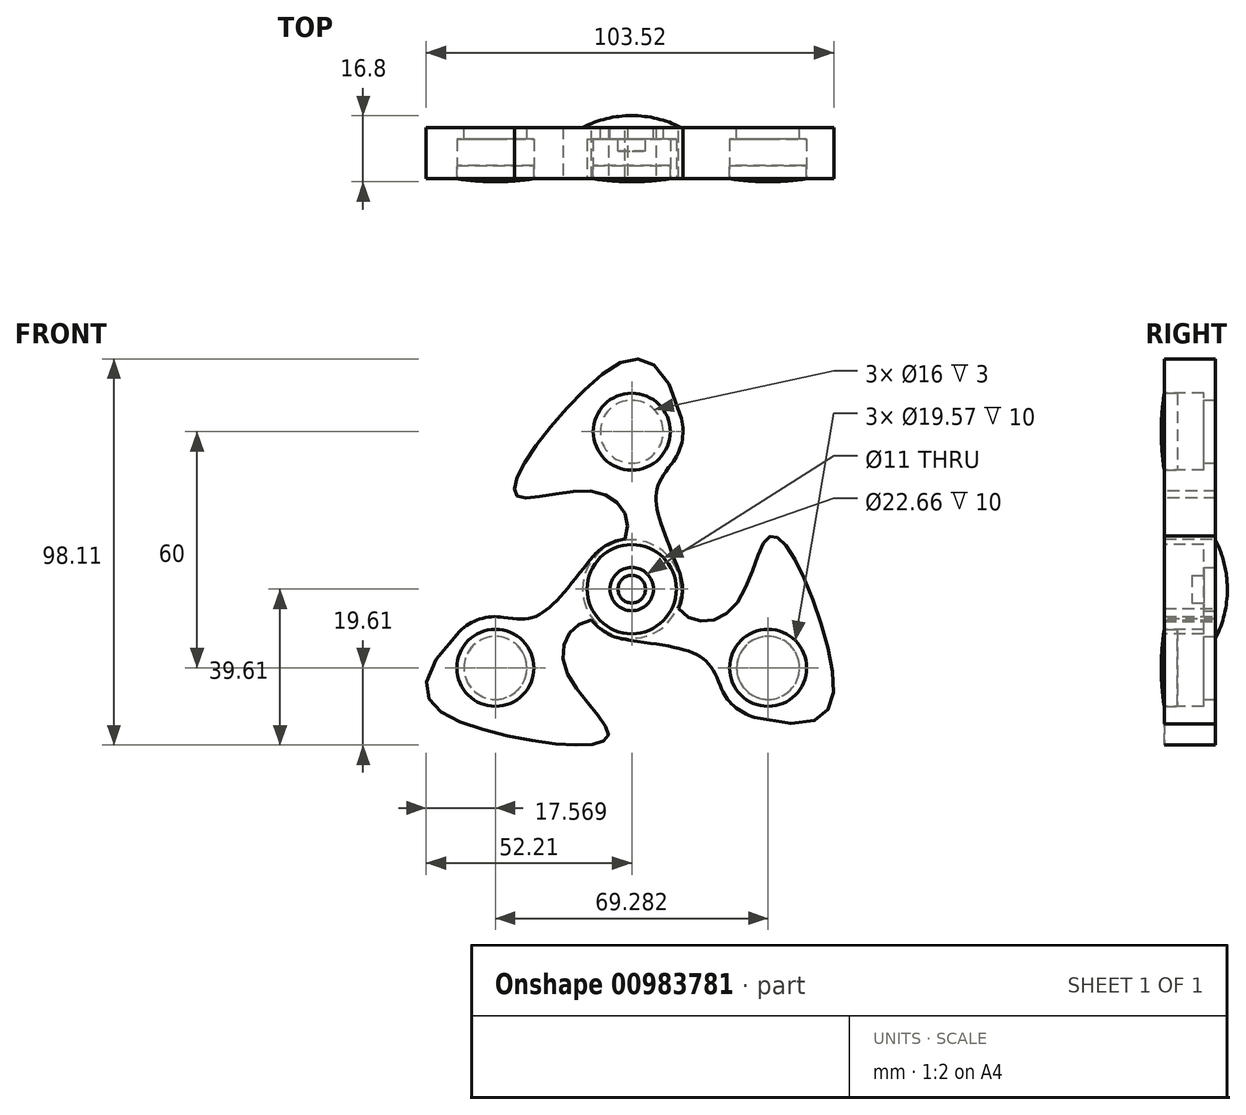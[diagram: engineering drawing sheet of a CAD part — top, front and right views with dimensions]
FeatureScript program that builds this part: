
annotation { "Feature Type Name" : "Feature", "Feature Type Description" : "" }
export const myFeature = defineFeature(function(context is Context, id is Id, definition is map)
    precondition{}
    {
        {
            var Q0;
            Q0=qCreatedBy(makeId("Right.planeOp"),FACE);
            var sketch = newSketch(context, id + "F0", { "sketchPlane" : qUnion([Q0])});
            skLineSegment(sketch, "E0", {"start": v(55.37, 0) * mm, "end": v(-57.34, 0) * mm, "construction": true});
            skSolve(sketch);
        }
        {
            var Q0;
            Q0=qCreatedBy(makeId("Front.planeOp"),FACE);
            var sketch = newSketch(context, id + "F1", { "sketchPlane" : qUnion([Q0])});
            skArc(sketch, "E1", {"start": v(10.1, 31.81) * mm, "mid": v(12.7, 37.26) * mm, "end": v(12.57, 43.3) * mm});
            skArc(sketch, "E2", {"start": v(-12.75, -1.81) * mm, "mid": v(3.2, -12.47) * mm, "end": v(12.04, 4.56) * mm});
            skFitSpline(sketch, "E3", {"points": [v(12.57, 43.3) * mm, v(-13, 49.56) * mm, v(-29.24, 23.79) * mm, v(-8.86, 24.65) * mm, v(-1.57, 13.14) * mm, v(-12.75, -1.81) * mm], "startDerivative": vector(-80.86, 308.24) * mm, "endDerivative": vector(8.65, -60.88) * mm});
            skFitSpline(sketch, "E4", {"points": [v(10.1, 31.81) * mm, v(6.13, 23.11) * mm, v(12.04, 4.56) * mm], "startDerivative": vector(-18.49, -22.8) * mm, "endDerivative": vector(14.68, -38.75) * mm});
            skCircle(sketch, "E5", {"center": v(0, 0) * mm, "radius": 5.5 * mm});
            skCircle(sketch, "E6", {"center": v(0, 40) * mm, "radius": 8 * mm});
            skSolve(sketch);
        }
        {
            var Q0;
            Q0 = qSketchRegion(id + "F1", true);
            extrude(context, id + "F2", {"entities" : qUnion([Q0]), "depth" : 13 * mm, "offsetDistance" : 25 * mm});
        }
        {
            var Q0;
            Q0=makeQuery(id+"F2.opExtrude","SWEPT_BODY",BODY,{"disambiguationData":[OSD([sQuery(id+"F1.wireOp",EDGE,"E1"),sQuery(id+"F1.wireOp",EDGE,"E2"),sQuery(id+"F1.wireOp",EDGE,"E3"),sQuery(id+"F1.wireOp",EDGE,"E4"),sQuery(id+"F1.wireOp",EDGE,"E5"),sQuery(id+"F1.wireOp",EDGE,"E6")])]});
            var Q1;
            Q1=sQuery(id+"F0.wireOp",EDGE,"E0");
            circularPattern(context, id + "F3", {"operationType" : NewBodyOperationType.ADD, "entities" : qUnion([Q0]), "axis" : qUnion([Q1]), "angle" : 360 * degree, "instanceCount" : 3, "equalSpace" : true});
        }
        {
            var Q0;
            {var subQ0=makeQuery(id+"F2.opExtrude","CAP_FACE",FACE,{"disambiguationData":[OSD([sQuery(id+"F1.wireOp",EDGE,"E1"),sQuery(id+"F1.wireOp",EDGE,"E2"),sQuery(id+"F1.wireOp",EDGE,"E3"),sQuery(id+"F1.wireOp",EDGE,"E4"),sQuery(id+"F1.wireOp",EDGE,"E5"),sQuery(id+"F1.wireOp",EDGE,"E6")])],"isStart":false});Q0=makeQuery(id+"F3.boolean.opBoolean","MERGE",FACE,{"derivedFrom":[subQ0,makeQuery(id+"F3.opPattern","COPY",FACE,{"derivedFrom":subQ0,"instanceName":"1"}),makeQuery(id+"F3.opPattern","COPY",FACE,{"derivedFrom":subQ0,"instanceName":"2"})]});}
            var sketch = newSketch(context, id + "F4", { "sketchPlane" : qUnion([Q0])});
            skCircle(sketch, "E7", {"center": v(0, 0) * mm, "radius": 11.33 * mm});
            skCircle(sketch, "E8.0", {"center": v(0, 40) * mm, "radius": 8 * mm, "construction": true});
            skCircle(sketch, "E9", {"center": v(0, 40) * mm, "radius": 9.79 * mm});
            skCircle(sketch, "E10", {"center": v(-34.64, -20) * mm, "radius": 9.79 * mm});
            skCircle(sketch, "E11", {"center": v(34.64, -20) * mm, "radius": 9.79 * mm});
            skCircle(sketch, "E12.0", {"center": v(-34.64, -20) * mm, "radius": 8 * mm, "construction": true});
            skCircle(sketch, "E13.0", {"center": v(34.64, -20) * mm, "radius": 8 * mm, "construction": true});
            skSolve(sketch);
        }
        {
            var Q0;
            Q0 = qSketchRegion(id + "F4", true);
            extrude(context, id + "F5", {"entities" : qUnion([Q0]), "operationType" : NewBodyOperationType.REMOVE, "oppositeDirection" : true, "depth" : 10 * mm, "offsetDistance" : 25 * mm});
        }
        {
            var Q0;
            Q0=qCreatedBy(makeId("Right.planeOp"),FACE);
            var sketch = newSketch(context, id + "F6", { "sketchPlane" : qUnion([Q0])});
            skPoint(sketch, "E14.0", {"position": v(0, 40) * mm});
            skLineSegment(sketch, "E15.0.0", {"start": v(-13, 11.33) * mm, "end": v(-13, -11.33) * mm, "construction": true});
            skFitSpline(sketch, "E15.0.1", {"points": [v(-13, 1.74) * mm, v(-13, 0.56) * mm, v(-13, -0.63) * mm, v(-13, -1.81) * mm], "construction": true});
            skLineSegment(sketch, "E15.0.2", {"start": v(-13, -4.88) * mm, "end": v(-13, 4.56) * mm, "construction": true});
            skFitSpline(sketch, "E15.0.3", {"points": [v(-13, 4.56) * mm, v(-13, 12.16) * mm, v(-13, 22.98) * mm, v(-13, 28.68) * mm, v(-13, 31.81) * mm], "construction": true});
            skLineSegment(sketch, "E16.0", {"start": v(-3, 30.21) * mm, "end": v(-3, 49.78) * mm, "construction": true});
            skLineSegment(sketch, "E17", {"start": v(-13, 49.78) * mm, "end": v(-3, 49.78) * mm, "construction": true});
            skLineSegment(sketch, "E18", {"start": v(-3, 30.21) * mm, "end": v(-9.72, 30.21) * mm, "construction": true});
            skLineSegment(sketch, "E19", {"start": v(-9.72, 49.78) * mm, "end": v(-9.72, 40) * mm});
            skLineSegment(sketch, "E20", {"start": v(-9.72, 49.78) * mm, "end": v(-13, 49.78) * mm});
            skArc(sketch, "E21", {"start": v(-13, 49.78) * mm, "mid": v(-13.6, 44.9) * mm, "end": v(-13.8, 40) * mm});
            skPoint(sketch, "E15.0.4.end.orphan", {"position": v(-13, 43.3) * mm});
            skPoint(sketch, "E22.trimOffspring.end.orphan", {"position": v(-13, 31.81) * mm});
            skLineSegment(sketch, "E23.0", {"start": v(0, 32) * mm, "end": v(0, 48) * mm, "construction": true});
            skFitSpline(sketch, "E24.0.1", {"points": [v(-13, 1.74) * mm, v(-13, 0.56) * mm, v(-13, -0.63) * mm, v(-13, -1.81) * mm], "construction": true});
            skFitSpline(sketch, "E24.0.3", {"points": [v(-13, 4.56) * mm, v(-13, 12.16) * mm, v(-13, 22.98) * mm, v(-13, 28.68) * mm, v(-13, 31.81) * mm], "construction": true});
            skLineSegment(sketch, "E24.0.4", {"start": v(-13, 31.81) * mm, "end": v(-13, 43.3) * mm, "construction": true});
            skLineSegment(sketch, "E25", {"start": v(0, 40) * mm, "end": v(-13.8, 40) * mm, "construction": true});
            skLineSegment(sketch, "E26", {"start": v(-9.72, 40) * mm, "end": v(-13.8, 40) * mm});
            skSolve(sketch);
        }
        {
            var Q0;
            Q0 = qSketchRegion(id + "F6", true);
            var Q1;
            Q1=sQuery(id+"F6.wireOp",EDGE,"E25");
            revolve(context, id + "F7", {"surfaceOperationType" : NewSurfaceOperationType.NEW, "entities" : qUnion([Q0]), "axis" : qUnion([Q1]), "revolveType" : RevolveType.FULL});
        }
        {
            var Q0;
            Q0=makeQuery(id+"F7.opRevolve","SWEPT_BODY",BODY,{"disambiguationData":[OSD([sQuery(id+"F6.wireOp",EDGE,"E19"),sQuery(id+"F6.wireOp",EDGE,"E20"),sQuery(id+"F6.wireOp",EDGE,"E21"),sQuery(id+"F6.wireOp",EDGE,"E26")])]});
            var Q1;
            Q1=sQuery(id+"F0.wireOp",EDGE,"E0");
            circularPattern(context, id + "F8", {"entities" : qUnion([Q0]), "axis" : qUnion([Q1]), "angle" : 360 * degree, "instanceCount" : 3, "equalSpace" : true});
        }
        {
            var Q0;
            Q0=qCreatedBy(makeId("Right.planeOp"),FACE);
            var sketch = newSketch(context, id + "F9", { "sketchPlane" : qUnion([Q0])});
            skLineSegment(sketch, "E27", {"start": v(-6, 0) * mm, "end": v(-6, 3.5) * mm});
            skLineSegment(sketch, "E28", {"start": v(-6, 3.5) * mm, "end": v(-3, 3.5) * mm});
            skLineSegment(sketch, "E29", {"start": v(-3, 3.5) * mm, "end": v(-3, 5.5) * mm});
            skLineSegment(sketch, "E30", {"start": v(-3, 5.5) * mm, "end": v(0, 5.5) * mm});
            skLineSegment(sketch, "E31", {"start": v(0, 5.5) * mm, "end": v(0, 12.5) * mm});
            skArc(sketch, "E32", {"start": v(3, 0) * mm, "mid": v(2.24, 6.43) * mm, "end": v(0, 12.5) * mm});
            skLineSegment(sketch, "E33", {"start": v(3, 0) * mm, "end": v(-6, 0) * mm});
            skLineSegment(sketch, "E34", {"start": v(36.57, 0) * mm, "end": v(-25.05, 0) * mm, "construction": true});
            skSolve(sketch);
        }
        {
            var Q0;
            Q0 = qSketchRegion(id + "F9", true);
            var Q1;
            Q1=sQuery(id+"F9.wireOp",EDGE,"E34");
            revolve(context, id + "F10", {"surfaceOperationType" : NewSurfaceOperationType.NEW, "entities" : qUnion([Q0]), "axis" : qUnion([Q1]), "revolveType" : RevolveType.FULL});
        }
    });
